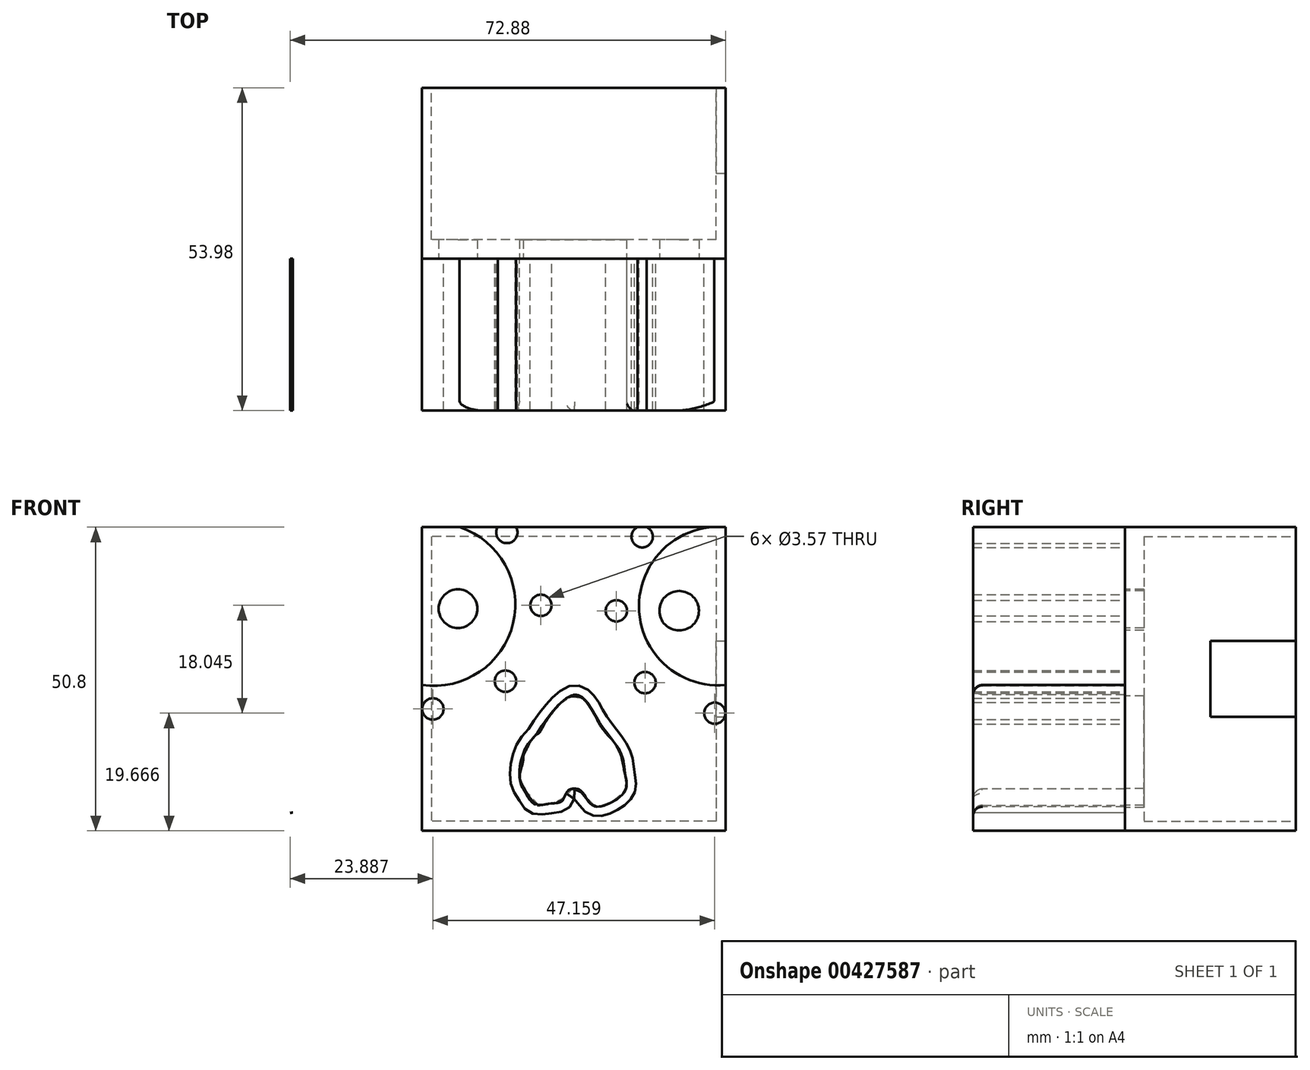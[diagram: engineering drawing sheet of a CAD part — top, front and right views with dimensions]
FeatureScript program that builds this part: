
annotation { "Feature Type Name" : "Feature", "Feature Type Description" : "" }
export const myFeature = defineFeature(function(context is Context, id is Id, definition is map)
    precondition{}
    {
        {
            var Q0;
            Q0=qCreatedBy(makeId("Front.planeOp"),FACE);
            var sketch = newSketch(context, id + "F0", { "sketchPlane" : qUnion([Q0])});
            skLineSegment(sketch, "E0.bottom", {"start": v(-25.26, 45.29) * mm, "end": v(25.54, 45.29) * mm});
            skLineSegment(sketch, "E0.top", {"start": v(-25.26, -5.51) * mm, "end": v(25.54, -5.51) * mm});
            skLineSegment(sketch, "E0.left", {"start": v(-25.26, 45.29) * mm, "end": v(-25.26, -5.51) * mm});
            skLineSegment(sketch, "E0.right", {"start": v(25.54, 45.29) * mm, "end": v(25.54, -5.51) * mm});
            skSolve(sketch);
        }
        {
            var Q0;
            Q0=makeQuery(id+"F0.imprint","IMPRINT",FACE,{"disambiguationData":[TD([[makeQuery(id+"F0.imprint","IMPRINT",EDGE,{"derivedFrom":sQuery(id+"F0.wireOp",EDGE,"E0.bottom")}),-1.0]])]});
            extrude(context, id + "F1", {"entities" : qUnion([Q0]), "depth" : 28.57 * mm});
        }
        {
            var Q0;
            Q0=makeQuery(id+"F1.opExtrude","CAP_FACE",FACE,{"disambiguationData":[OSD([sQuery(id+"F0.wireOp",EDGE,"E0.bottom"),sQuery(id+"F0.wireOp",EDGE,"E0.top"),sQuery(id+"F0.wireOp",EDGE,"E0.left"),sQuery(id+"F0.wireOp",EDGE,"E0.right")])],"isStart":true});
            var sketch = newSketch(context, id + "F2", { "sketchPlane" : qUnion([Q0])});
            skLineSegment(sketch, "E1.0", {"start": v(-23.95, 43.7) * mm, "end": v(23.67, 43.7) * mm});
            skLineSegment(sketch, "E1.1", {"start": v(-23.95, 43.7) * mm, "end": v(-23.95, -3.92) * mm});
            skLineSegment(sketch, "E1.2", {"start": v(-23.95, -3.92) * mm, "end": v(23.67, -3.92) * mm});
            skLineSegment(sketch, "E1.3", {"start": v(23.67, 43.7) * mm, "end": v(23.67, -3.92) * mm});
            skSolve(sketch);
        }
        {
            var Q0;
            Q0 = qSketchRegion(id + "F2", true);
            extrude(context, id + "F3", {"entities" : qUnion([Q0]), "operationType" : NewBodyOperationType.REMOVE, "oppositeDirection" : true, "depth" : 25.4 * mm});
        }
        {
            var Q0;
            Q0=makeQuery(id+"F1.opExtrude","SWEPT_FACE",FACE,{"disambiguationData":[OSD([sQuery(id+"F0.wireOp",EDGE,"E0.right")])]});
            var sketch = newSketch(context, id + "F4", { "sketchPlane" : qUnion([Q0])});
            skLineSegment(sketch, "E2", {"start": v(-14.29, -5.51) * mm, "end": v(-14.29, 13.54) * mm, "construction": true});
            skPoint(sketch, "E2.endSnap0", {"position": v(-14.29, 45.29) * mm});
            skLineSegment(sketch, "E3", {"start": v(-14.29, 45.29) * mm, "end": v(-14.29, 26.24) * mm, "construction": true});
            skLineSegment(sketch, "E4", {"start": v(-14.29, 26.24) * mm, "end": v(0, 26.24) * mm});
            skLineSegment(sketch, "E5", {"start": v(-14.29, 13.54) * mm, "end": v(0, 13.54) * mm});
            skLineSegment(sketch, "E6", {"start": v(0, 13.54) * mm, "end": v(0, 26.24) * mm});
            skLineSegment(sketch, "E7", {"start": v(-14.29, 26.24) * mm, "end": v(-14.29, 13.54) * mm});
            skSolve(sketch);
        }
        {
            var Q0;
            Q0 = qSketchRegion(id + "F4", true);
            extrude(context, id + "F5", {"entities" : qUnion([Q0]), "operationType" : NewBodyOperationType.REMOVE, "endBound" : BoundingType.UP_TO_NEXT, "oppositeDirection" : true, "depth" : 25.4 * mm});
        }
        {
            var Q0;
            Q0=makeQuery(id+"F1.opExtrude","CAP_FACE",FACE,{"disambiguationData":[OSD([sQuery(id+"F0.wireOp",EDGE,"E0.bottom"),sQuery(id+"F0.wireOp",EDGE,"E0.top"),sQuery(id+"F0.wireOp",EDGE,"E0.left"),sQuery(id+"F0.wireOp",EDGE,"E0.right")])],"isStart":false});
            var sketch = newSketch(context, id + "F6", { "sketchPlane" : qUnion([Q0])});
            skFitSpline(sketch, "E8", {"points": [v(-51.38, 22.9) * mm, v(-49.5, 44.92) * mm, v(-41.95, 65.68) * mm, v(-28.73, 74.5) * mm, v(-14.9, 78.9) * mm, v(9.01, 80.15) * mm, v(26.63, 76.38) * mm, v(40.47, 66.94) * mm, v(48.65, 54.99) * mm, v(50.54, 41.15) * mm, v(51.17, 28.57) * mm, v(50.97, 23.38) * mm, v(42.65, 22.78) * mm, v(39.28, 20.6) * mm, v(45.42, 20.2) * mm, v(51.96, 19.02) * mm, v(56.71, 16.44) * mm, v(59.3, 10.9) * mm, v(59.3, 6.14) * mm, v(56.71, 0) * mm, v(52.36, -1.79) * mm, v(45.82, -3.37) * mm, v(39.08, -8.53) * mm, v(36.7, -11.9) * mm, v(34.92, -17.44) * mm, v(34.52, -22.8) * mm, v(33.87, -28.14) * mm, v(32.38, -33.19) * mm, v(28.82, -36.75) * mm, v(24.96, -39.42) * mm, v(16.35, -42.39) * mm, v(5.96, -43.58) * mm, v(-3.55, -43.87) * mm, v(-11.56, -42.69) * mm, v(-19.28, -41.2) * mm, v(-26.4, -38.23) * mm, v(-31.16, -33.78) * mm, v(-33.53, -28.43) * mm, v(-34.42, -22.8) * mm, v(-34.13, -16.86) * mm, v(-35.9, -10.92) * mm, v(-39.17, -7.35) * mm, v(-41.85, -4.09) * mm, v(-45.7, -2.3) * mm, v(-47.34, -2.51) * mm, v(-49.94, -2.14) * mm, v(-52.16, -1.77) * mm, v(-56.25, 1.05) * mm, v(-58.1, 5.06) * mm, v(-58.4, 7.8) * mm, v(-58.62, 11.6) * mm, v(-55.8, 15.38) * mm, v(-52.6, 18.42) * mm, v(-48.75, 19.6) * mm, v(-42.3, 19.76) * mm, v(-39.17, 19.98) * mm, v(-40.58, 21.46) * mm, v(-43.4, 22.2) * mm, v(-46.67, 22.65) * mm, v(-51.38, 22.9) * mm]});
            skLineSegment(sketch, "E9", {"start": v(-47.34, -2.51) * mm, "end": v(-45.7, -2.3) * mm});
            skCircle(sketch, "E10", {"center": v(-23.27, 32.36) * mm, "radius": 13.62 * mm});
            skCircle(sketch, "E11", {"center": v(24.27, 32.06) * mm, "radius": 13.24 * mm});
            skCircle(sketch, "E12", {"center": v(-23.46, 49.57) * mm, "radius": 1.78 * mm});
            skCircle(sketch, "E13", {"center": v(-39.9, 32) * mm, "radius": 1.78 * mm});
            skCircle(sketch, "E14", {"center": v(-5.38, 32.2) * mm, "radius": 1.78 * mm});
            skCircle(sketch, "E15", {"center": v(-23.45, 14.87) * mm, "radius": 1.78 * mm});
            skCircle(sketch, "E16", {"center": v(-35.6, 44.38) * mm, "radius": 1.78 * mm});
            skCircle(sketch, "E17", {"center": v(-11.07, 44.38) * mm, "radius": 1.78 * mm});
            skCircle(sketch, "E18", {"center": v(-11.31, 19.5) * mm, "radius": 1.78 * mm});
            skCircle(sketch, "E19", {"center": v(-35.12, 19.98) * mm, "radius": 1.78 * mm});
            skCircle(sketch, "E20", {"center": v(23.7, 48.86) * mm, "radius": 1.78 * mm});
            skCircle(sketch, "E21", {"center": v(7.25, 31.29) * mm, "radius": 1.78 * mm});
            skCircle(sketch, "E22", {"center": v(41.78, 31.5) * mm, "radius": 1.78 * mm});
            skCircle(sketch, "E23", {"center": v(23.7, 14.16) * mm, "radius": 1.78 * mm});
            skCircle(sketch, "E24", {"center": v(11.57, 43.67) * mm, "radius": 1.78 * mm});
            skCircle(sketch, "E25", {"center": v(36.08, 43.67) * mm, "radius": 1.78 * mm});
            skCircle(sketch, "E26", {"center": v(35.85, 18.8) * mm, "radius": 1.78 * mm});
            skCircle(sketch, "E27", {"center": v(12.04, 19.27) * mm, "radius": 1.78 * mm});
            skFitSpline(sketch, "E28", {"points": [v(-2.08, 48) * mm, v(-4.78, 52.05) * mm, v(-8.53, 55.65) * mm, v(-11.83, 56.7) * mm, v(-19.63, 57.15) * mm, v(-22.93, 57.6) * mm, v(-25.03, 60.9) * mm, v(-25.78, 63.15) * mm, v(-24.28, 65.4) * mm, v(-21.43, 66.6) * mm, v(-17.38, 66.3) * mm, v(-15.13, 66) * mm, v(-11.53, 64.05) * mm, v(-8.53, 61.8) * mm, v(-6.28, 58.8) * mm, v(-3.58, 55.35) * mm, v(-1.48, 51.75) * mm, v(0, 49.2) * mm, v(3.02, 54.3) * mm, v(5.27, 58.65) * mm, v(7.82, 61.5) * mm, v(10.21, 63.3) * mm, v(13.66, 64.8) * mm, v(15.76, 65.7) * mm, v(20.11, 66.6) * mm, v(21.31, 66.74) * mm, v(22.81, 66.44) * mm, v(25.21, 65.1) * mm, v(26.86, 61.8) * mm, v(26.11, 58.05) * mm, v(23.26, 56.55) * mm, v(17.41, 56.55) * mm, v(13.66, 56.85) * mm, v(9.47, 55.65) * mm, v(7.82, 53.7) * mm, v(4.97, 50.4) * mm, v(2.57, 46.8) * mm, v(0, 45.87) * mm, v(-2.08, 48) * mm]});
            skFitSpline(sketch, "E29", {"points": [v(0, 17.2) * mm, v(2.82, 15.3) * mm, v(4.73, 12.12) * mm, v(7.99, 7.5) * mm, v(8.7, 4.1) * mm, v(8.78, 1.31) * mm, v(5.76, -1.07) * mm, v(3.22, -1.23) * mm, v(1.4, 0.91) * mm, v(0, 1.47) * mm, v(-0.82, 1.18) * mm, v(-1.54, 0) * mm, v(-1.99, -0.65) * mm, v(-4.23, -1.03) * mm, v(-6.48, -1.07) * mm, v(-7.87, 0.77) * mm, v(-8.73, 2.27) * mm, v(-8.96, 4.48) * mm, v(-8.8, 5.83) * mm, v(-7.72, 8.72) * mm, v(-6.26, 10.48) * mm, v(-5.4, 11.76) * mm, v(0, 17.2) * mm]});
            skLineSegment(sketch, "E30", {"start": v(-47.36, 11.62) * mm, "end": v(-45.3, 8.06) * mm});
            skLineSegment(sketch, "E31", {"start": v(-45.3, 8.06) * mm, "end": v(-41.48, 6.71) * mm});
            skLineSegment(sketch, "E32", {"start": v(-41.48, 6.71) * mm, "end": v(-44.06, 4.99) * mm});
            skLineSegment(sketch, "E33", {"start": v(-44.06, 4.99) * mm, "end": v(-44.06, 0.86) * mm});
            skLineSegment(sketch, "E34", {"start": v(-44.06, 0.86) * mm, "end": v(-46.09, 2.32) * mm});
            skLineSegment(sketch, "E35", {"start": v(-46.09, 2.32) * mm, "end": v(-47.36, 2.32) * mm});
            skLineSegment(sketch, "E36.MirrorCS", {"start": v(-48.64, 2.32) * mm, "end": v(-47.36, 2.32) * mm});
            skLineSegment(sketch, "E37.MirrorCS", {"start": v(-50.66, 0.86) * mm, "end": v(-48.64, 2.32) * mm});
            skLineSegment(sketch, "E38.MirrorCS", {"start": v(-50.66, 4.99) * mm, "end": v(-50.66, 0.86) * mm});
            skLineSegment(sketch, "E39.MirrorCS", {"start": v(-53.25, 6.71) * mm, "end": v(-50.66, 4.99) * mm});
            skLineSegment(sketch, "E40.MirrorCS", {"start": v(-47.36, 11.62) * mm, "end": v(-49.42, 8.06) * mm});
            skLineSegment(sketch, "E41.MirrorCS", {"start": v(-49.42, 8.06) * mm, "end": v(-53.25, 6.71) * mm});
            skLineSegment(sketch, "E42", {"start": v(43.97, 12.44) * mm, "end": v(46.03, 8.87) * mm});
            skLineSegment(sketch, "E43", {"start": v(46.03, 8.87) * mm, "end": v(49.86, 7.52) * mm});
            skLineSegment(sketch, "E44", {"start": v(49.86, 7.52) * mm, "end": v(47.27, 5.8) * mm});
            skLineSegment(sketch, "E45", {"start": v(47.27, 5.8) * mm, "end": v(47.27, 1.68) * mm});
            skLineSegment(sketch, "E46", {"start": v(47.27, 1.68) * mm, "end": v(45.24, 3.14) * mm});
            skLineSegment(sketch, "E47", {"start": v(45.24, 3.14) * mm, "end": v(43.97, 3.14) * mm});
            skLineSegment(sketch, "E48.MirrorCS", {"start": v(43.97, 3.14) * mm, "end": v(42.7, 3.14) * mm});
            skLineSegment(sketch, "E49.MirrorCS", {"start": v(40.67, 1.68) * mm, "end": v(42.7, 3.14) * mm});
            skLineSegment(sketch, "E50.MirrorCS", {"start": v(40.67, 5.8) * mm, "end": v(40.67, 1.68) * mm});
            skLineSegment(sketch, "E51.MirrorCS", {"start": v(38.08, 7.52) * mm, "end": v(40.67, 5.8) * mm});
            skLineSegment(sketch, "E52.MirrorCS", {"start": v(41.9, 8.87) * mm, "end": v(43.97, 12.44) * mm});
            skLineSegment(sketch, "E53.MirrorCS", {"start": v(41.9, 8.87) * mm, "end": v(38.08, 7.52) * mm});
            skFitSpline(sketch, "E54", {"points": [v(-29.84, -16) * mm, v(-30.24, -11.99) * mm, v(-28.9, -10.39) * mm, v(-25.03, -9.32) * mm, v(-21.16, -9.85) * mm, v(-20.36, -11.19) * mm, v(-18.62, -11.05) * mm, v(-15.68, -9.85) * mm, v(-11, -11.05) * mm, v(-10.34, -11.05) * mm, v(-6.46, -8.78) * mm, v(-4.32, -8.25) * mm, v(0, -9.99) * mm, v(1.82, -10.39) * mm, v(5.03, -8.92) * mm, v(10.64, -11.19) * mm, v(16.25, -9.32) * mm, v(19.86, -12.12) * mm, v(25.47, -8.65) * mm, v(30.95, -14.4) * mm, v(31.35, -23.88) * mm, v(27.07, -29.9) * mm, v(21.33, -29.9) * mm, v(18.52, -31.76) * mm, v(12.1, -31.63) * mm, v(9.04, -34.97) * mm, v(3.16, -35.1) * mm, v(0, -32.3) * mm, v(-2.32, -34.17) * mm, v(-6.33, -34.57) * mm, v(-10.47, -31.1) * mm, v(-14.21, -32.83) * mm, v(-19.82, -29.62) * mm, v(-25.57, -30.16) * mm, v(-30.38, -25.35) * mm, v(-29.84, -16) * mm]});
            skFitSpline(sketch, "E55", {"points": [v(-24.31, -12.77) * mm, v(-26.33, -13.3) * mm, v(-26.7, -16.51) * mm, v(-24.43, -18.42) * mm, v(-21.87, -18.06) * mm, v(-21.63, -15.56) * mm, v(-24.31, -12.77) * mm]});
            skFitSpline(sketch, "E56", {"points": [v(-15.38, -13.12) * mm, v(-17.88, -14.9) * mm, v(-18.42, -17.23) * mm, v(-17.23, -18.9) * mm, v(-14.67, -19.67) * mm, v(-12.53, -18.78) * mm, v(-12.53, -17) * mm, v(-13.42, -14.55) * mm, v(-15.38, -13.12) * mm]});
            skFitSpline(sketch, "E57", {"points": [v(-4.43, -12.88) * mm, v(-6.93, -13.42) * mm, v(-8.42, -15.2) * mm, v(-8.78, -17.35) * mm, v(-7.7, -19.2) * mm, v(-5.2, -19.79) * mm, v(-3.78, -19.67) * mm, v(-2.83, -19.25) * mm, v(-2.11, -16.57) * mm, v(-2.11, -15.5) * mm, v(-3.3, -13.78) * mm, v(-3.84, -12.94) * mm, v(-4.43, -12.88) * mm]});
            skFitSpline(sketch, "E58", {"points": [v(5.44, -13) * mm, v(3.12, -15.38) * mm, v(2.47, -18) * mm, v(4.31, -19.5) * mm, v(6.63, -19.55) * mm, v(7.88, -19.55) * mm, v(9.07, -19.2) * mm, v(8.42, -16.63) * mm, v(7.82, -14.67) * mm, v(6.52, -13) * mm, v(5.44, -13) * mm]});
            skFitSpline(sketch, "E59", {"points": [v(16.45, -13.12) * mm, v(14.49, -13.9) * mm, v(13.12, -15.2) * mm, v(12.82, -17) * mm, v(13.48, -19.13) * mm, v(14.43, -19.79) * mm, v(17.29, -19.79) * mm, v(18, -19.13) * mm, v(18.36, -18.18) * mm, v(18.54, -17.17) * mm, v(18.54, -16.22) * mm, v(17.94, -15.44) * mm, v(17.7, -14.9) * mm, v(17.1, -13.9) * mm, v(16.45, -13.12) * mm]});
            skFitSpline(sketch, "E60", {"points": [v(26.03, -13) * mm, v(24.73, -12.94) * mm, v(23.06, -14.31) * mm, v(22.88, -15.62) * mm, v(23.35, -17.04) * mm, v(24.96, -18.06) * mm, v(27.52, -17.47) * mm, v(27.7, -15.8) * mm, v(27.28, -14.25) * mm, v(26.03, -13) * mm]});
            skFitSpline(sketch, "E61", {"points": [v(26.2, -26.88) * mm, v(25.78, -27.06) * mm, v(24.88, -27.17) * mm, v(24.22, -27.14) * mm, v(23.42, -26.75) * mm, v(22.97, -26.35) * mm, v(22.73, -25.1) * mm, v(22.73, -24.57) * mm, v(22.5, -24.2) * mm, v(22.3, -23.54) * mm, v(22.3, -22.72) * mm, v(22.47, -22.19) * mm, v(23.08, -21.44) * mm, v(23.77, -21.23) * mm, v(25.17, -20.94) * mm, v(26.13, -21.02) * mm, v(26.92, -21.28) * mm, v(27.5, -21.87) * mm, v(27.8, -22.42) * mm, v(27.87, -22.77) * mm, v(27.95, -23.22) * mm, v(27.95, -23.25) * mm, v(27.66, -24.04) * mm, v(27.42, -24.47) * mm, v(27.1, -24.76) * mm, v(26.63, -25.29) * mm, v(26.47, -26.27) * mm, v(26.2, -26.88) * mm]});
            skFitSpline(sketch, "E62", {"points": [v(15.68, -22.72) * mm, v(14.2, -22.95) * mm, v(13.35, -23.25) * mm, v(12.8, -23.83) * mm, v(12.63, -24.44) * mm, v(12.84, -25.5) * mm, v(13.08, -26.24) * mm, v(13.37, -27.62) * mm, v(13.64, -28.87) * mm, v(14.83, -29.24) * mm, v(16.03, -29.24) * mm, v(16.6, -29.16) * mm, v(17.27, -28.87) * mm, v(17.56, -28.44) * mm, v(17.67, -28.04) * mm, v(17.9, -27.3) * mm, v(18.41, -26.32) * mm, v(19.9, -26.08) * mm, v(19.47, -24.2) * mm, v(19.44, -23.8) * mm, v(18.89, -22.85) * mm, v(18.36, -22.56) * mm, v(17.43, -22.42) * mm, v(15.84, -22.42) * mm, v(15.68, -22.72) * mm]});
            skFitSpline(sketch, "E63", {"points": [v(5.95, -31.63) * mm, v(3.11, -28.22) * mm, v(2.36, -27.47) * mm, v(2.92, -23.83) * mm, v(4.9, -23.03) * mm, v(8.3, -23.83) * mm, v(9.25, -25.49) * mm, v(9.16, -27.1) * mm, v(7.84, -29.08) * mm, v(6.99, -30.59) * mm, v(5.95, -31.63) * mm]});
            skFitSpline(sketch, "E64", {"points": [v(-5.55, -23.03) * mm, v(-7.85, -23.24) * mm, v(-8.66, -24.2) * mm, v(-8.98, -26.04) * mm, v(-8.52, -27.7) * mm, v(-8.24, -28.23) * mm, v(-7.88, -28.7) * mm, v(-6.86, -30) * mm, v(-6, -31.27) * mm, v(-5.3, -31.6) * mm, v(-4.6, -31.6) * mm, v(-3.42, -31.06) * mm, v(-3.1, -30.25) * mm, v(-2.54, -29.3) * mm, v(-1.65, -27.91) * mm, v(-1.27, -26.78) * mm, v(-1.16, -26.21) * mm, v(-1.16, -25.58) * mm, v(-1.94, -24.52) * mm, v(-3.99, -23.2) * mm, v(-4.95, -23.07) * mm, v(-5.55, -23.03) * mm]});
            skFitSpline(sketch, "E65", {"points": [v(-15.62, -22.5) * mm, v(-16.94, -22.71) * mm, v(-18.1, -23.2) * mm, v(-18.58, -23.83) * mm, v(-18.42, -24.52) * mm, v(-18.17, -25.4) * mm, v(-17.8, -26.43) * mm, v(-17.48, -27.35) * mm, v(-17.29, -27.8) * mm, v(-17.04, -28.48) * mm, v(-16.4, -28.86) * mm, v(-15.56, -28.99) * mm, v(-14.64, -28.83) * mm, v(-13.44, -28.55) * mm, v(-13.06, -28.42) * mm, v(-12.53, -26.81) * mm, v(-12.3, -26.06) * mm, v(-12.3, -25.33) * mm, v(-12.43, -24.07) * mm, v(-12.72, -23.53) * mm, v(-13.35, -23.2) * mm, v(-14.51, -22.59) * mm, v(-15.62, -22.5) * mm]});
            skFitSpline(sketch, "E66", {"points": [v(-25.23, -21.08) * mm, v(-26.46, -21.17) * mm, v(-27.16, -22.18) * mm, v(-27.25, -23.2) * mm, v(-26.56, -24.52) * mm, v(-26.4, -25.27) * mm, v(-25.93, -25.93) * mm, v(-25.26, -26.37) * mm, v(-24.82, -26.78) * mm, v(-24.13, -27.03) * mm, v(-23.56, -27.2) * mm, v(-23.15, -27.2) * mm, v(-22.27, -26.78) * mm, v(-21.86, -26.3) * mm, v(-21.42, -25.58) * mm, v(-21.14, -24.95) * mm, v(-21.04, -24.2) * mm, v(-21.23, -23.2) * mm, v(-21.9, -22.3) * mm, v(-23.56, -21.55) * mm, v(-25.23, -21.08) * mm]});
            skLineSegment(sketch, "E67", {"start": v(-19.69, -11.35) * mm, "end": v(-18.42, -17.23) * mm});
            skLineSegment(sketch, "E68", {"start": v(-12.53, -17) * mm, "end": v(-10.34, -11.05) * mm});
            skLineSegment(sketch, "E69", {"start": v(-8.98, -26.04) * mm, "end": v(-8.98, -31.98) * mm});
            skLineSegment(sketch, "E70", {"start": v(-1.27, -26.78) * mm, "end": v(-1.27, -33.15) * mm});
            skLineSegment(sketch, "E71", {"start": v(1.82, -10.39) * mm, "end": v(2.47, -18) * mm});
            skLineSegment(sketch, "E72", {"start": v(9.07, -19.2) * mm, "end": v(10.64, -11.19) * mm});
            skLineSegment(sketch, "E73", {"start": v(2.36, -27.47) * mm, "end": v(2.36, -34.48) * mm});
            skLineSegment(sketch, "E74", {"start": v(9.16, -27.1) * mm, "end": v(9.04, -34.97) * mm});
            skLineSegment(sketch, "E75", {"start": v(23.35, -17.04) * mm, "end": v(21.13, -11.65) * mm});
            skLineSegment(sketch, "E76", {"start": v(27.7, -15.8) * mm, "end": v(28.17, -9.8) * mm});
            skLineSegment(sketch, "E77", {"start": v(-8.78, -17.35) * mm, "end": v(-8.78, -10.17) * mm});
            skLineSegment(sketch, "E78", {"start": v(-2.11, -16.57) * mm, "end": v(-2.11, -9) * mm});
            skLineSegment(sketch, "E79", {"start": v(-27.25, -23.2) * mm, "end": v(-27.25, -29.6) * mm});
            skLineSegment(sketch, "E80", {"start": v(-21.04, -24.2) * mm, "end": v(-21.04, -29.5) * mm});
            skSolve(sketch);
        }
        {
            var Q0;
            Q0=makeQuery(id+"F6.imprint","IMPRINT",FACE,{"disambiguationData":[TD([[makeQuery(id+"F6.imprint","IMPRINT",EDGE,{"derivedFrom":sQuery(id+"F6.wireOp",EDGE,"E8")}),-1.0]])]});
            var Q1;
            Q1=makeQuery(id+"F6.imprint","IMPRINT",FACE,{"disambiguationData":[TD([[makeQuery(id+"F6.imprint","IMPRINT",EDGE,{"derivedFrom":sQuery(id+"F6.wireOp",EDGE,"E14")}),-1.0]])]});
            extrude(context, id + "F7", {"entities" : qUnion([Q0, Q1]), "depth" : 25.4 * mm});
        }
        {
            var Q0;
            Q0=makeQuery(id+"F7.opExtrude","CAP_EDGE",EDGE,{"disambiguationData":[OSD([sQuery(id+"F6.wireOp",EDGE,"E11")])],"isStart":false});
            var Q1;
            Q1=makeQuery(id+"F7.opExtrude","CAP_EDGE",EDGE,{"disambiguationData":[OSD([sQuery(id+"F6.wireOp",EDGE,"E10")])],"isStart":false});
            var Q2;
            Q2=makeQuery(id+"F7.opExtrude","CAP_EDGE",EDGE,{"disambiguationData":[OSD([sQuery(id+"F6.wireOp",EDGE,"E28")])],"isStart":false});
            var Q3;
            Q3=makeQuery(id+"F7.opExtrude","CAP_EDGE",EDGE,{"disambiguationData":[OSD([sQuery(id+"F6.wireOp",EDGE,"E29")])],"isStart":false});
            fillet(context, id + "F8", {"entities" : qUnion([Q0, Q1, Q2, Q3]), "radius" : 1.59 * mm, "tangentPropagation" : true, "allowEdgeOverflow" : false});
        }
        {
            var Q0;
            Q0=makeQuery(id+"F1.opExtrude","CAP_FACE",FACE,{"disambiguationData":[OSD([sQuery(id+"F0.wireOp",EDGE,"E0.bottom"),sQuery(id+"F0.wireOp",EDGE,"E0.top"),sQuery(id+"F0.wireOp",EDGE,"E0.left"),sQuery(id+"F0.wireOp",EDGE,"E0.right")])],"isStart":false});
            var sketch = newSketch(context, id + "F9", { "sketchPlane" : qUnion([Q0])});
            skCircle(sketch, "E81", {"center": v(-19.25, 31.65) * mm, "radius": 3.23 * mm});
            skCircle(sketch, "E82", {"center": v(17.75, 31.3) * mm, "radius": 3.3 * mm});
            skFitSpline(sketch, "E83", {"points": [v(-8.35, 6.23) * mm, v(-8.32, 6.98) * mm, v(-7.75, 8.21) * mm, v(-6.52, 10.35) * mm, v(-5.73, 10.8) * mm, v(-4.71, 12.5) * mm, v(-3.36, 14.4) * mm, v(-1.56, 16.43) * mm, v(0, 17) * mm, v(1.36, 16.77) * mm, v(3.17, 14.74) * mm, v(4.97, 11.48) * mm, v(7.44, 8.55) * mm, v(8.46, 5.06) * mm, v(8.9, 2.81) * mm, v(8.68, 1) * mm, v(5.98, -1.02) * mm, v(3.5, -1.47) * mm, v(1.25, 1.23) * mm, v(0, 1.52) * mm, v(-0.79, 1.23) * mm, v(-1.94, -0.64) * mm, v(-3.53, -0.93) * mm, v(-5.9, -1.14) * mm, v(-8.43, 2.03) * mm, v(-8.93, 3.75) * mm, v(-8.35, 6.23) * mm]});
            skSolve(sketch);
        }
        {
            var Q0;
            Q0=makeQuery(id+"F9.imprint","IMPRINT",FACE,{"disambiguationData":[TD([[makeQuery(id+"F9.imprint","IMPRINT",EDGE,{"derivedFrom":sQuery(id+"F9.wireOp",EDGE,"E81")}),1.0]])]});
            var Q1;
            Q1=makeQuery(id+"F9.imprint","IMPRINT",FACE,{"disambiguationData":[TD([[makeQuery(id+"F9.imprint","IMPRINT",EDGE,{"derivedFrom":sQuery(id+"F9.wireOp",EDGE,"E82")}),1.0]])]});
            var Q2;
            Q2=makeQuery(id+"F9.imprint","IMPRINT",FACE,{"disambiguationData":[TD([[makeQuery(id+"F9.imprint","IMPRINT",EDGE,{"derivedFrom":sQuery(id+"F9.wireOp",EDGE,"E83")}),-1.0]])]});
            var Q3;
            Q3=sQuery(id+"F9.wireOp",EDGE,"E82");
            var Q4;
            Q4=sQuery(id+"F9.wireOp",EDGE,"E81");
            extrude(context, id + "F10", {"entities" : qUnion([Q0, Q1, Q2]), "operationType" : NewBodyOperationType.REMOVE, "surfaceEntities" : qUnion([Q3, Q4]), "oppositeDirection" : true, "depth" : 25.4 * mm});
        }
    });
